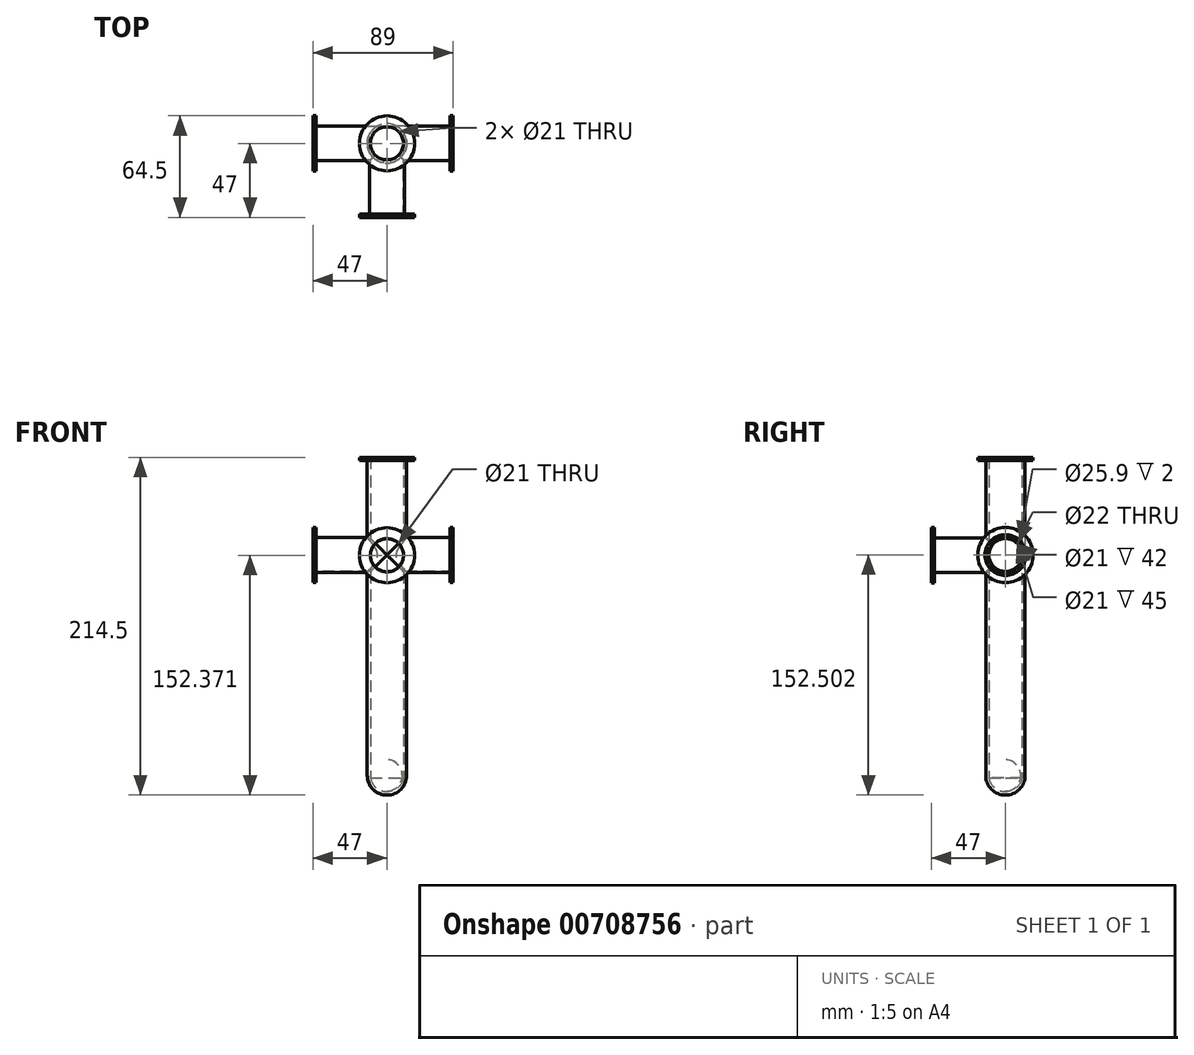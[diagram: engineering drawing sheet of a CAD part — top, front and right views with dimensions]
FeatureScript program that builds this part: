
annotation { "Feature Type Name" : "Feature", "Feature Type Description" : "" }
export const myFeature = defineFeature(function(context is Context, id is Id, definition is map)
    precondition{}
    {
        {
            var Q0;
            Q0=qCreatedBy(makeId("Front.planeOp"),FACE);
            var sketch = newSketch(context, id + "F0", { "sketchPlane" : qUnion([Q0])});
            skArc(sketch, "E0", {"start": v(-12.5, -7.77) * mm, "mid": v(0, -20.27) * mm, "end": v(12.5, -7.77) * mm});
            skLineSegment(sketch, "E1", {"start": v(-12.5, -7.77) * mm, "end": v(-12.5, 192.23) * mm});
            skLineSegment(sketch, "E2", {"start": v(-12.5, 192.23) * mm, "end": v(12.5, 192.23) * mm});
            skLineSegment(sketch, "E3", {"start": v(12.5, 192.23) * mm, "end": v(12.5, -7.77) * mm});
            skLineSegment(sketch, "E4", {"start": v(0, -20.27) * mm, "end": v(0, 192.23) * mm});
            skLineSegment(sketch, "E5", {"start": v(10.5, 192.23) * mm, "end": v(10.5, -9.27) * mm});
            skArc(sketch, "E6", {"start": v(-9.71, -8.42) * mm, "mid": v(0, -17.97) * mm, "end": v(10.5, -9.27) * mm});
            skSolve(sketch);
        }
        {
            var Q0;
            {var subQ5=sQuery(id+"F0.wireOp",EDGE,"E3");Q0=makeQuery(id+"F0.imprint","IMPRINT",FACE,{"disambiguationData":[TD([[makeQuery(id+"F0.imprint","IMPRINT",EDGE,{"derivedFrom":subQ5}),-1.0]])]});}
            var Q1;
            Q1=sQuery(id+"F0.wireOp",EDGE,"E4");
            revolve(context, id + "F1", {"surfaceOperationType" : NewSurfaceOperationType.NEW, "entities" : qUnion([Q0]), "axis" : qUnion([Q1]), "revolveType" : RevolveType.FULL});
        }
        {
            var Q0;
            Q0=makeQuery(id+"F1.opRevolve","SWEPT_FACE",FACE,{"disambiguationData":[OSD([sQuery(id+"F0.wireOp",EDGE,"E2")])]});
            var sketch = newSketch(context, id + "F2", { "sketchPlane" : qUnion([Q0])});
            skCircle(sketch, "E7", {"center": v(0, 0) * mm, "radius": 17.5 * mm});
            skCircle(sketch, "E8", {"center": v(0, 0) * mm, "radius": 10 * mm});
            skSolve(sketch);
        }
        {
            var Q0;
            Q0=makeQuery(id+"F2.imprint","IMPRINT",FACE,{"disambiguationData":[TD([[makeQuery(id+"F2.imprint","IMPRINT",EDGE,{"derivedFrom":sQuery(id+"F2.wireOp",EDGE,"E7")}),1.0]])]});
            var Q1;
            {var subQ0=sQuery(id+"F0.wireOp",EDGE,"E2");Q1=makeQuery(id+"F2.imprint","IMPRINT",FACE,{"disambiguationData":[TD([[makeQuery(id+"F2.imprint","IMPRINT",EDGE,{"derivedFrom":makeQuery(id+"F1.opRevolve","SWEPT_EDGE",EDGE,{"disambiguationData":[OSD([subQ0,sQuery(id+"F0.wireOp",EDGE,"E3")])]})}),-1.0]])]});}
            extrude(context, id + "F3", {"entities" : qUnion([Q0, Q1]), "operationType" : NewBodyOperationType.ADD, "depth" : 2 * mm, "offsetDistance" : 25 * mm});
        }
        {
            var Q0;
            Q0=qCreatedBy(makeId("Right.planeOp"),FACE);
            var sketch = newSketch(context, id + "F4", { "sketchPlane" : qUnion([Q0])});
            skCircle(sketch, "E9", {"center": v(0, 132.23) * mm, "radius": 11 * mm});
            skCircle(sketch, "E10", {"center": v(0, 132.23) * mm, "radius": 9.5 * mm});
            skSolve(sketch);
        }
        {
            var Q0;
            Q0 = qSketchRegion(id + "F4", true);
            extrude(context, id + "F5", {"entities" : qUnion([Q0]), "operationType" : NewBodyOperationType.ADD, "depth" : 40 * mm, "offsetDistance" : 25 * mm});
        }
        {
            var Q0;
            Q0 = qSketchRegion(id + "F4", true);
            extrude(context, id + "F6", {"entities" : qUnion([Q0]), "operationType" : NewBodyOperationType.ADD, "oppositeDirection" : true, "depth" : 45 * mm, "offsetDistance" : 25 * mm});
        }
        {
            var Q0;
            Q0=qCreatedBy(makeId("Front.planeOp"),FACE);
            var sketch = newSketch(context, id + "F7", { "sketchPlane" : qUnion([Q0])});
            skCircle(sketch, "E11", {"center": v(0, 132.1) * mm, "radius": 11 * mm});
            skCircle(sketch, "E12", {"center": v(0, 132.1) * mm, "radius": 9 * mm});
            skSolve(sketch);
        }
        {
            var Q0;
            Q0 = qSketchRegion(id + "F7", true);
            extrude(context, id + "F8", {"entities" : qUnion([Q0]), "operationType" : NewBodyOperationType.ADD, "depth" : 45 * mm, "offsetDistance" : 25 * mm});
        }
        {
            var Q0;
            Q0=makeQuery(id+"F3.opExtrude","CAP_FACE",FACE,{"disambiguationData":[OSD([sQuery(id+"F0.wireOp",EDGE,"E2"),sQuery(id+"F0.wireOp",EDGE,"E5"),sQuery(id+"F2.wireOp",EDGE,"E7")])],"isStart":false});
            var sketch = newSketch(context, id + "F9", { "sketchPlane" : qUnion([Q0])});
            skCircle(sketch, "E13", {"center": v(0, 0) * mm, "radius": 10.5 * mm});
            skSolve(sketch);
        }
        {
            var Q0;
            Q0 = qSketchRegion(id + "F9", true);
            extrude(context, id + "F10", {"entities" : qUnion([Q0]), "operationType" : NewBodyOperationType.REMOVE, "oppositeDirection" : true, "depth" : 150 * mm, "offsetDistance" : 25 * mm});
        }
        {
            var Q0;
            Q0=makeQuery(id+"F8.opExtrude","CAP_FACE",FACE,{"disambiguationData":[OSD([sQuery(id+"F7.wireOp",EDGE,"E11"),sQuery(id+"F7.wireOp",EDGE,"E12")])],"isStart":false});
            var sketch = newSketch(context, id + "F11", { "sketchPlane" : qUnion([Q0])});
            skCircle(sketch, "E14", {"center": v(0, 132.1) * mm, "radius": 10.5 * mm});
            skCircle(sketch, "E15", {"center": v(0, 132.1) * mm, "radius": 17.5 * mm});
            skSolve(sketch);
        }
        {
            var Q0;
            Q0=makeQuery(id+"F11.imprint","IMPRINT",FACE,{"disambiguationData":[TD([[makeQuery(id+"F11.imprint","IMPRINT",EDGE,{"derivedFrom":sQuery(id+"F11.wireOp",EDGE,"E15")}),1.0]])]});
            var Q1;
            Q1=makeQuery(id+"F11.imprint","IMPRINT",FACE,{"disambiguationData":[TD([[makeQuery(id+"F11.imprint","IMPRINT",EDGE,{"derivedFrom":sQuery(id+"F11.wireOp",EDGE,"E14")}),-1.0]])]});
            extrude(context, id + "F12", {"entities" : qUnion([Q0, Q1]), "operationType" : NewBodyOperationType.ADD, "depth" : 2 * mm, "offsetDistance" : 25 * mm});
        }
        {
            var Q0;
            Q0=makeQuery(id+"F5.opExtrude","CAP_FACE",FACE,{"disambiguationData":[OSD([sQuery(id+"F4.wireOp",EDGE,"E9"),sQuery(id+"F4.wireOp",EDGE,"E10")])],"isStart":false});
            var sketch = newSketch(context, id + "F13", { "sketchPlane" : qUnion([Q0])});
            skCircle(sketch, "E16", {"center": v(0, 132.23) * mm, "radius": 12.95 * mm});
            skCircle(sketch, "E17", {"center": v(0, 132.23) * mm, "radius": 17.5 * mm});
            skSolve(sketch);
        }
        {
            var Q0;
            Q0=makeQuery(id+"F13.imprint","IMPRINT",FACE,{"disambiguationData":[TD([[makeQuery(id+"F13.imprint","IMPRINT",EDGE,{"derivedFrom":sQuery(id+"F13.wireOp",EDGE,"E16")}),-1.0]])]});
            var Q1;
            Q1=makeQuery(id+"F13.imprint","IMPRINT",FACE,{"disambiguationData":[TD([[makeQuery(id+"F13.imprint","IMPRINT",EDGE,{"derivedFrom":makeQuery(id+"F5.opExtrude","CAP_EDGE",EDGE,{"disambiguationData":[OSD([sQuery(id+"F4.wireOp",EDGE,"E9")])],"isStart":false})}),1.0]])]});
            extrude(context, id + "F14", {"entities" : qUnion([Q0, Q1]), "operationType" : NewBodyOperationType.ADD, "depth" : 2 * mm, "offsetDistance" : 25 * mm});
        }
        {
            var Q0;
            Q0=makeQuery(id+"F6.opExtrude","CAP_FACE",FACE,{"disambiguationData":[OSD([sQuery(id+"F4.wireOp",EDGE,"E9"),sQuery(id+"F4.wireOp",EDGE,"E10")])],"isStart":false});
            var sketch = newSketch(context, id + "F15", { "sketchPlane" : qUnion([Q0])});
            skCircle(sketch, "E18", {"center": v(0, 132.23) * mm, "radius": 17.5 * mm});
            skCircle(sketch, "E19", {"center": v(0, 132.23) * mm, "radius": 10.5 * mm});
            skSolve(sketch);
        }
        {
            var Q0;
            Q0=makeQuery(id+"F15.imprint","IMPRINT",FACE,{"disambiguationData":[TD([[makeQuery(id+"F15.imprint","IMPRINT",EDGE,{"derivedFrom":sQuery(id+"F15.wireOp",EDGE,"E19")}),1.0]])]});
            var Q1;
            Q1=makeQuery(id+"F15.imprint","IMPRINT",FACE,{"disambiguationData":[TD([[makeQuery(id+"F15.imprint","IMPRINT",EDGE,{"derivedFrom":sQuery(id+"F15.wireOp",EDGE,"E18")}),1.0]])]});
            extrude(context, id + "F16", {"entities" : qUnion([Q0, Q1]), "operationType" : NewBodyOperationType.ADD, "depth" : 2 * mm, "offsetDistance" : 25 * mm});
        }
        {
            var Q0;
            Q0=makeQuery(id+"F16.opExtrude","CAP_FACE",FACE,{"disambiguationData":[OSD([sQuery(id+"F15.wireOp",EDGE,"E18"),sQuery(id+"F15.wireOp",EDGE,"E19")])],"isStart":false});
            var sketch = newSketch(context, id + "F17", { "sketchPlane" : qUnion([Q0])});
            skCircle(sketch, "E20", {"center": v(0, 132.23) * mm, "radius": 10.5 * mm});
            skSolve(sketch);
        }
        {
            var Q0;
            Q0 = qSketchRegion(id + "F17", true);
            extrude(context, id + "F18", {"entities" : qUnion([Q0]), "operationType" : NewBodyOperationType.REMOVE, "endBound" : BoundingType.THROUGH_ALL, "oppositeDirection" : true, "depth" : 25 * mm, "offsetDistance" : 25 * mm});
        }
        {
            var Q0;
            Q0=makeQuery(id+"F12.opExtrude","CAP_FACE",FACE,{"disambiguationData":[OSD([sQuery(id+"F11.wireOp",EDGE,"E14"),sQuery(id+"F11.wireOp",EDGE,"E15")])],"isStart":false});
            var sketch = newSketch(context, id + "F19", { "sketchPlane" : qUnion([Q0])});
            skCircle(sketch, "E21", {"center": v(0, 132.1) * mm, "radius": 10.5 * mm});
            skSolve(sketch);
        }
        {
            var Q0;
            Q0 = qSketchRegion(id + "F19", true);
            extrude(context, id + "F20", {"entities" : qUnion([Q0]), "operationType" : NewBodyOperationType.REMOVE, "oppositeDirection" : true, "depth" : 48 * mm, "offsetDistance" : 25 * mm});
        }
    });
